# Revit family: TY5111
name_source: partatom
category: Sprinklers
revit_build: Autodesk Revit 2016 (Build: 20150220_1215(x64)
units: mm (PartAtom-declared; Revit-internal decimal feet)

## family parameters
Always vertical = Yes
Cut with Voids When Loaded = No
Maintain Annotation Orientation = No
OmniClass Number = 23.65.70.17.11.24
OmniClass Title = Fire Fighting Sprinkler Heads
Part Type = Normal
Room Calculation Point = No
Round Connector Dimension = Use Diameter
Shared = No
Work Plane-Based = No

## types (15) — shared parameters
COBie = Yes
COBie.Type = Yes
COBie.Type.AssetType = Fixed
COBie.Type.Category = Pr_70_55_97_84:Sprinklers
COBie.Type.DurationUnit = year
COBie.Type.Manufacturer = Tyco Fire Protection Products
COBie.Type.Material = Bronze
COBie.Type.Shape = Cylinder
COBie.Type.Size = 3/4"(DN20)
COBie.Type.WarrantyGuarantorParts = http://tycofsbp.com
Coverage = Standard
K-Factor = 159.8191
Manufacturer = Tyco Fire Protection Products
Manufacturer URL = www.tyco-fire.com
Model = ELO-231
Nominal Diameter 1 = 20 mm
Orifice = Extra Large
Orifice Size = 16 mm
Outside Diameter 1 = 27 mm
Response = Standard
SIN No = TY5111
Takeout 1 = 71 mm
Technical Data Sheet No = TFP340
zero-valued in all types: COBie.Type.NominalHeight, COBie.Type.NominalLength, COBie.Type.NominalWidth, COBie.Type.ReplacementCost, Style Id

## per-type parameters (varying)
| type | COBie.Component.Description | COBie.Component.Name | COBie.Type.Colour | COBie.Type.Finish | COBie.Type.ModelNumber | COBie.Type.ModelReference | Part No | Temperature Rating |
| ELO-231 Upright Brass 165°F/74°C 11.2K ¾" NPT_50-110-1-165 | ELO-231 Wet Upright  73.9°C K160 DN20 NPT Br | Sprinklers:Upright_165 | Yellow | Natural Brass | 50-110-1-165 | ELO-231 Wet Upright  73.9°C K160 DN20 NPT Br | 50-110-1-165 | 74 °C |
| ELO-231 Upright Brass 212°F/100°C 11.2K ¾" NPT_50-110-1-212 | ELO-231 Wet Upright  100°C K160 DN20 NPT Br | Sprinklers:Upright_212 | Yellow | Natural Brass | 50-110-1-212 | ELO-231 Wet Upright  100°C K160 DN20 NPT Br | 50-110-1-212 | 100 °C |
| ELO-231 Upright Brass 286°F/141°C 11.2K ¾" NPT_50-110-1-286 | ELO-231 Wet Upright  141.1°C K160 DN20 NPT Br | Sprinklers:Upright_286 | Yellow | Natural Brass | 50-110-1-286 | ELO-231 Wet Upright  141.1°C K160 DN20 NPT Br | 50-110-1-286 | 141 °C |
| ELO-231 Upright Wax 165°F/74°C 11.2K ¾" NPT_50-110-6-165 | ELO-231 Wet Upright  73.9°C K160 DN20 NPT Wx | Sprinklers:Upright_165 | Gray | Wax Coated | 50-110-6-165 | ELO-231 Wet Upright  73.9°C K160 DN20 NPT Wx | 50-110-6-165 | 74 °C |
| ELO-231 Upright Wax 212°F/100°C 11.2K ¾" NPT_50-110-6-212 | ELO-231 Wet Upright  100°C K160 DN20 NPT Wx | Sprinklers:Upright_212 | Gray | Wax Coated | 50-110-6-212 | ELO-231 Wet Upright  100°C K160 DN20 NPT Wx | 50-110-6-212 | 100 °C |
| ELO-231 Upright Wax 286°F/141°C 11.2K ¾" NPT_50-110-6-286 | ELO-231 Wet Upright  141.1°C K160 DN20 NPT Wx | Sprinklers:Upright_286 | Gray | Wax Coated | 50-110-6-286 | ELO-231 Wet Upright  141.1°C K160 DN20 NPT Wx | 50-110-6-286 | 141 °C |
| ELO-231 Upright Lead 165°F/74°C 11.2K ¾" NPT_50-110-7-165 | ELO-231 Wet Upright  73.9°C K160 DN20 NPT Lead | Sprinklers:Upright_165 | Gray | Lead Coated | 50-110-7-165 | ELO-231 Wet Upright  73.9°C K160 DN20 NPT Lead | 50-110-7-165 | 74 °C |
| ELO-231 Upright Lead 212°F/100°C 11.2K ¾" NPT_50-110-7-212 | ELO-231 Wet Upright  100°C K160 DN20 NPT Lead | Sprinklers:Upright_212 | Gray | Lead Coated | 50-110-7-212 | ELO-231 Wet Upright  100°C K160 DN20 NPT Lead | 50-110-7-212 | 100 °C |
| ELO-231 Upright Lead 286°F/141°C 11.2K ¾" NPT_50-110-7-286 | ELO-231 Wet Upright  141.1°C K160 DN20 NPT Lead | Sprinklers:Upright_286 | Gray | Lead Coated | 50-110-7-286 | ELO-231 Wet Upright  141.1°C K160 DN20 NPT Lead | 50-110-7-286 | 141 °C |
| ELO-231 Upright Wax Over Lead 165°F/74°C 11.2K ¾" NPT_50-110-8-165 | ELO-231 Wet Upright  73.9°C K160 DN20 NPT WoL | Sprinklers:Upright_165 | Gray | Wax Over Lead | 50-110-8-165 | ELO-231 Wet Upright  73.9°C K160 DN20 NPT WoL | 50-110-8-165 | 74 °C |
| ELO-231 Upright Wax Over Lead 212°F/100°C 11.2K ¾" NPT_50-110-8-212 | ELO-231 Wet Upright  100°C K160 DN20 NPT WoL | Sprinklers:Upright_212 | Gray | Wax Over Lead | 50-110-8-212 | ELO-231 Wet Upright  100°C K160 DN20 NPT WoL | 50-110-8-212 | 100 °C |
| ELO-231 Upright Wax Over Lead 286°F/141°C 11.2K ¾" NPT_50-110-8-286 | ELO-231 Wet Upright  141.1°C K160 DN20 NPT WoL | Sprinklers:Upright_286 | Gray | Wax Over Lead | 50-110-8-286 | ELO-231 Wet Upright  141.1°C K160 DN20 NPT WoL | 50-110-8-286 | 141 °C |
| ELO-231 Upright Chrome 165°F/74°C 11.2K ¾" NPT_50-110-9-165 | ELO-231 Wet Upright  73.9°C K160 DN20 NPT Chr | Sprinklers:Upright_165 | Silver | Chrome Plated | 50-110-9-165 | ELO-231 Wet Upright  73.9°C K160 DN20 NPT Chr | 50-110-9-165 | 74 °C |
| ELO-231 Upright Chrome 212°F/100°C 11.2K ¾" NPT_50-110-9-212 | ELO-231 Wet Upright  100°C K160 DN20 NPT Chr | Sprinklers:Upright_212 | Silver | Chrome Plated | 50-110-9-212 | ELO-231 Wet Upright  100°C K160 DN20 NPT Chr | 50-110-9-212 | 100 °C |
| ELO-231 Upright Chrome 286°F/141°C 11.2K ¾" NPT_50-110-9-286 | ELO-231 Wet Upright  141.1°C K160 DN20 NPT Chr | Sprinklers:Upright_286 | Silver | Chrome Plated | 50-110-9-286 | ELO-231 Wet Upright  141.1°C K160 DN20 NPT Chr | 50-110-9-286 | 141 °C |

note: column(s) folded — value = type name in every type: Description

## geometry (parser evidence)
native form markers: Blend x2, Sweep x66
no freeform markers — native parametric forms only
